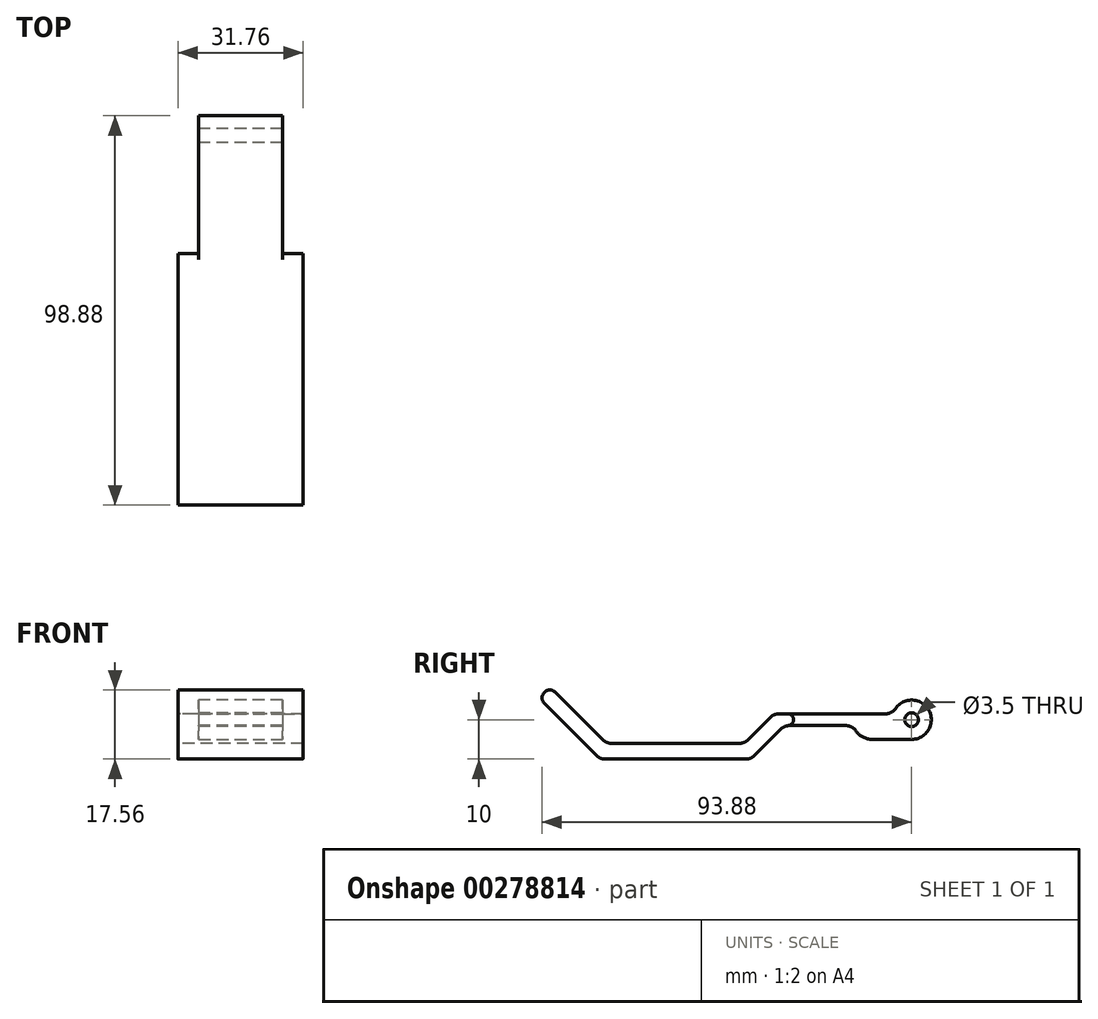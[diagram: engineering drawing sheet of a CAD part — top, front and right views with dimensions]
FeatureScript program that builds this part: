
annotation { "Feature Type Name" : "Feature", "Feature Type Description" : "" }
export const myFeature = defineFeature(function(context is Context, id is Id, definition is map)
    precondition{}
    {
        {
            var Q0;
            Q0=qCreatedBy(makeId("Right.planeOp"),FACE);
            var sketch = newSketch(context, id + "F0", { "sketchPlane" : qUnion([Q0])});
            skCircle(sketch, "E0", {"center": v(0, 0) * mm, "radius": 1.75 * mm});
            skLineSegment(sketch, "E1", {"start": v(0, 0) * mm, "end": v(-10, 0) * mm, "construction": true});
            skLineSegment(sketch, "E2", {"start": v(-10, 0) * mm, "end": v(-60, 0) * mm, "construction": true});
            skPoint(sketch, "E3", {"position": v(-42.5, 0) * mm});
            skLineSegment(sketch, "E4", {"start": v(-60, 0) * mm, "end": v(-60, 34.1) * mm, "construction": true});
            skCircle(sketch, "E5", {"center": v(-10, 0) * mm, "radius": 5 * mm, "construction": true});
            skArc(sketch, "E6", {"start": v(-4.77, -1.5) * mm, "mid": v(5, 0) * mm, "end": v(-4.77, 1.5) * mm});
            skLineSegment(sketch, "E7", {"start": v(-4.77, 1.5) * mm, "end": v(-35, 1.5) * mm});
            skLineSegment(sketch, "E8", {"start": v(-4.77, -1.5) * mm, "end": v(-5.23, -1.5) * mm});
            skArc(sketch, "E9", {"start": v(-5.23, -1.5) * mm, "mid": v(-10, -5) * mm, "end": v(-14.77, -1.5) * mm});
            skLineSegment(sketch, "E10", {"start": v(-77.5, -6) * mm, "end": v(-42.5, -6) * mm});
            skPoint(sketch, "E11", {"position": v(-60, -6) * mm});
            skLineSegment(sketch, "E12", {"start": v(-35, 1.5) * mm, "end": v(-42.5, -6) * mm});
            skLineSegment(sketch, "E13", {"start": v(-14.77, -1.5) * mm, "end": v(-32.34, -1.5) * mm});
            skLineSegment(sketch, "E14", {"start": v(-32.34, -1.5) * mm, "end": v(-40.84, -10) * mm});
            skLineSegment(sketch, "E15", {"start": v(-40.84, -10) * mm, "end": v(-79.16, -10) * mm});
            skLineSegment(sketch, "E16", {"start": v(-77.5, -6) * mm, "end": v(-90.47, 6.97) * mm});
            skLineSegment(sketch, "E17", {"start": v(-79.16, -10) * mm, "end": v(-93.3, 4.14) * mm});
            skArc(sketch, "E18", {"start": v(-90.47, 6.97) * mm, "mid": v(-93.3, 6.97) * mm, "end": v(-93.3, 4.14) * mm});
            skSolve(sketch);
        }
        {
            var Q0;
            Q0 = qSketchRegion(id + "F0", true);
            extrude(context, id + "F1", {"entities" : qUnion([Q0]), "endBound" : BoundingType.SYMMETRIC, "depth" : 31.75 * mm});
        }
        {
            var Q0;
            Q0=makeQuery(id+"F1.opExtrude","CAP_FACE",FACE,{"disambiguationData":[OSD([sQuery(id+"F0.wireOp",EDGE,"E0"),sQuery(id+"F0.wireOp",EDGE,"E6"),sQuery(id+"F0.wireOp",EDGE,"E7"),sQuery(id+"F0.wireOp",EDGE,"E8"),sQuery(id+"F0.wireOp",EDGE,"E9"),sQuery(id+"F0.wireOp",EDGE,"E10"),sQuery(id+"F0.wireOp",EDGE,"E12"),sQuery(id+"F0.wireOp",EDGE,"E13"),sQuery(id+"F0.wireOp",EDGE,"E14"),sQuery(id+"F0.wireOp",EDGE,"E15"),sQuery(id+"F0.wireOp",EDGE,"E16"),sQuery(id+"F0.wireOp",EDGE,"E17"),sQuery(id+"F0.wireOp",EDGE,"E18")])],"isStart":false});
            var sketch = newSketch(context, id + "F2", { "sketchPlane" : qUnion([Q0])});
            skLineSegment(sketch, "E19", {"start": v(-10, -5) * mm, "end": v(0, -5) * mm});
            skArc(sketch, "E20.0", {"start": v(-5.23, -1.5) * mm, "mid": v(-7.04, -4.03) * mm, "end": v(-10, -5) * mm});
            skArc(sketch, "E20.1", {"start": v(-4.77, -1.5) * mm, "mid": v(-2.96, -4.03) * mm, "end": v(0, -5) * mm});
            skLineSegment(sketch, "E20.2", {"start": v(-4.77, -1.5) * mm, "end": v(-5.23, -1.5) * mm});
            skPoint(sketch, "E21.orphan", {"position": v(-14.77, -1.5) * mm});
            skPoint(sketch, "E22.orphan", {"position": v(-4.77, 1.5) * mm});
            skSolve(sketch);
        }
        {
            var Q0;
            Q0 = qSketchRegion(id + "F2", true);
            var Q1;
            Q1=makeQuery(id+"F1.opExtrude","CAP_FACE",FACE,{"disambiguationData":[OSD([sQuery(id+"F0.wireOp",EDGE,"E0"),sQuery(id+"F0.wireOp",EDGE,"E6"),sQuery(id+"F0.wireOp",EDGE,"E7"),sQuery(id+"F0.wireOp",EDGE,"E8"),sQuery(id+"F0.wireOp",EDGE,"E9"),sQuery(id+"F0.wireOp",EDGE,"E10"),sQuery(id+"F0.wireOp",EDGE,"E12"),sQuery(id+"F0.wireOp",EDGE,"E13"),sQuery(id+"F0.wireOp",EDGE,"E14"),sQuery(id+"F0.wireOp",EDGE,"E15"),sQuery(id+"F0.wireOp",EDGE,"E16"),sQuery(id+"F0.wireOp",EDGE,"E17"),sQuery(id+"F0.wireOp",EDGE,"E18")])],"isStart":true});
            extrude(context, id + "F3", {"entities" : qUnion([Q0]), "operationType" : NewBodyOperationType.ADD, "endBound" : BoundingType.UP_TO_SURFACE, "oppositeDirection" : true, "endBoundEntityFace" : qUnion([Q1]), "depth" : 25 * mm});
        }
        {
            var Q0;
            Q0=makeQuery(id+"F1.opExtrude","SWEPT_EDGE",EDGE,{"disambiguationData":[OSD([sQuery(id+"F0.wireOp",EDGE,"E6"),sQuery(id+"F0.wireOp",EDGE,"E7")])]});
            var Q1;
            Q1=makeQuery(id+"F1.opExtrude","SWEPT_EDGE",EDGE,{"disambiguationData":[OSD([sQuery(id+"F0.wireOp",EDGE,"E9"),sQuery(id+"F0.wireOp",EDGE,"E13")])]});
            var Q2;
            Q2=makeQuery(id+"F1.opExtrude","SWEPT_EDGE",EDGE,{"disambiguationData":[OSD([sQuery(id+"F0.wireOp",EDGE,"E10"),sQuery(id+"F0.wireOp",EDGE,"E16")])]});
            var Q3;
            Q3=makeQuery(id+"F1.opExtrude","SWEPT_EDGE",EDGE,{"disambiguationData":[OSD([sQuery(id+"F0.wireOp",EDGE,"E15"),sQuery(id+"F0.wireOp",EDGE,"E17")])]});
            var Q4;
            Q4=makeQuery(id+"F1.opExtrude","SWEPT_EDGE",EDGE,{"disambiguationData":[OSD([sQuery(id+"F0.wireOp",EDGE,"E14"),sQuery(id+"F0.wireOp",EDGE,"E15")])]});
            var Q5;
            Q5=makeQuery(id+"F1.opExtrude","SWEPT_EDGE",EDGE,{"disambiguationData":[OSD([sQuery(id+"F0.wireOp",EDGE,"E13"),sQuery(id+"F0.wireOp",EDGE,"E14")])]});
            var Q6;
            Q6=makeQuery(id+"F1.opExtrude","SWEPT_EDGE",EDGE,{"disambiguationData":[OSD([sQuery(id+"F0.wireOp",EDGE,"E10"),sQuery(id+"F0.wireOp",EDGE,"E12")])]});
            var Q7;
            Q7=makeQuery(id+"F1.opExtrude","SWEPT_EDGE",EDGE,{"disambiguationData":[OSD([sQuery(id+"F0.wireOp",EDGE,"E7"),sQuery(id+"F0.wireOp",EDGE,"E12")])]});
            fillet(context, id + "F4", {"entities" : qUnion([Q0, Q1, Q2, Q3, Q4, Q5, Q6, Q7]), "radius" : 3 * mm, "tangentPropagation" : true, "allowEdgeOverflow" : false});
        }
        {
            var Q0;
            Q0=qCreatedBy(makeId("Top.planeOp"),FACE);
            var sketch = newSketch(context, id + "F5", { "sketchPlane" : qUnion([Q0])});
            skLineSegment(sketch, "E23", {"start": v(0, 0) * mm, "end": v(0, -50.55) * mm, "construction": true});
            skLineSegment(sketch, "E24.0", {"start": v(15.88, -10) * mm, "end": v(15.88, 0) * mm, "construction": true});
            skPoint(sketch, "E25", {"position": v(0, -15) * mm});
            skPoint(sketch, "E26", {"position": v(0, -20) * mm});
            skLineSegment(sketch, "E27.0", {"start": v(-15.88, 5) * mm, "end": v(-15.88, -4.13) * mm, "construction": true});
            skLineSegment(sketch, "E28.bottom", {"start": v(-15.88, 5) * mm, "end": v(-10.87, 5) * mm});
            skLineSegment(sketch, "E28.top", {"start": v(-15.88, -30) * mm, "end": v(-10.87, -30) * mm});
            skLineSegment(sketch, "E28.left", {"start": v(-15.88, 5) * mm, "end": v(-15.88, -30) * mm});
            skLineSegment(sketch, "E28.right", {"start": v(-10.87, 5) * mm, "end": v(-10.87, -30) * mm});
            skLineSegment(sketch, "E29.MirrorCS", {"start": v(15.88, -30) * mm, "end": v(10.87, -30) * mm});
            skLineSegment(sketch, "E30.MirrorCS", {"start": v(10.87, 5) * mm, "end": v(10.87, -30) * mm});
            skLineSegment(sketch, "E31.MirrorCS", {"start": v(15.88, 5) * mm, "end": v(15.88, -30) * mm});
            skLineSegment(sketch, "E32.MirrorCS", {"start": v(15.88, 5) * mm, "end": v(10.87, 5) * mm});
            skSolve(sketch);
        }
        {
            var Q0;
            Q0 = qSketchRegion(id + "F5", true);
            extrude(context, id + "F6", {"entities" : qUnion([Q0]), "operationType" : NewBodyOperationType.REMOVE, "endBound" : BoundingType.THROUGH_ALL, "oppositeDirection" : true, "depth" : 25 * mm, "hasSecondDirection" : true, "secondDirectionBound" : SecondDirectionBoundingType.THROUGH_ALL, "secondDirectionOppositeDirection" : false, "secondDirectionDepth" : 25 * mm});
        }
        {
            var Q0;
            Q0=makeQuery(id+"F6.boolean.opBoolean","INTERSECT",EDGE,{"derivedFrom":[makeQuery(id+"F1.opExtrude","SWEPT_FACE",FACE,{"disambiguationData":[OSD([sQuery(id+"F0.wireOp",EDGE,"E13")])]}),makeQuery(id+"F6.opExtrude","SWEPT_FACE",FACE,{"disambiguationData":[OSD([sQuery(id+"F5.wireOp",EDGE,"E29.MirrorCS")])]})]});
            var Q1;
            Q1=makeQuery(id+"F6.boolean.opBoolean","INTERSECT",EDGE,{"derivedFrom":[makeQuery(id+"F1.opExtrude","SWEPT_FACE",FACE,{"disambiguationData":[OSD([sQuery(id+"F0.wireOp",EDGE,"E7")])]}),makeQuery(id+"F6.opExtrude","SWEPT_FACE",FACE,{"disambiguationData":[OSD([sQuery(id+"F5.wireOp",EDGE,"E29.MirrorCS")])]})]});
            var Q2;
            Q2=makeQuery(id+"F6.boolean.opBoolean","INTERSECT",EDGE,{"derivedFrom":[makeQuery(id+"F1.opExtrude","SWEPT_FACE",FACE,{"disambiguationData":[OSD([sQuery(id+"F0.wireOp",EDGE,"E7")])]}),makeQuery(id+"F6.opExtrude","SWEPT_FACE",FACE,{"disambiguationData":[OSD([sQuery(id+"F5.wireOp",EDGE,"E28.top")])]})]});
            var Q3;
            Q3=makeQuery(id+"F6.boolean.opBoolean","INTERSECT",EDGE,{"derivedFrom":[makeQuery(id+"F1.opExtrude","SWEPT_FACE",FACE,{"disambiguationData":[OSD([sQuery(id+"F0.wireOp",EDGE,"E13")])]}),makeQuery(id+"F6.opExtrude","SWEPT_FACE",FACE,{"disambiguationData":[OSD([sQuery(id+"F5.wireOp",EDGE,"E28.top")])]})]});
            fillet(context, id + "F7", {"entities" : qUnion([Q0, Q1, Q2, Q3]), "radius" : 1.5 * mm, "tangentPropagation" : true, "allowEdgeOverflow" : false});
        }
        {
            var Q0;
            Q0=makeQuery(id+"F6.boolean.opBoolean","COPY",FACE,{"derivedFrom":makeQuery(id+"F6.opExtrude","SWEPT_FACE",FACE,{"disambiguationData":[OSD([sQuery(id+"F5.wireOp",EDGE,"E30.MirrorCS")])]})});
            extrude(context, id + "F8", {"entities" : qUnion([Q0]), "operationType" : NewBodyOperationType.REMOVE, "oppositeDirection" : true, "depth" : 0.2 * mm});
        }
        {
            var Q0;
            Q0=makeQuery(id+"F6.boolean.opBoolean","COPY",FACE,{"derivedFrom":makeQuery(id+"F6.opExtrude","SWEPT_FACE",FACE,{"disambiguationData":[OSD([sQuery(id+"F5.wireOp",EDGE,"E28.right")])]})});
            extrude(context, id + "F9", {"entities" : qUnion([Q0]), "operationType" : NewBodyOperationType.REMOVE, "oppositeDirection" : true, "depth" : 0.2 * mm});
        }
    });
